# Revit family: Haworth_BeHold_Modular_AttachedLateral
name_source: partatom
category: Furniture Systems
revit_build: Autodesk Revit 2018 (Build: 20170223_1515(x64)
units: mm (PartAtom-declared; Revit-internal decimal feet)

## family parameters
Always vertical = Yes
Cut with Voids When Loaded = No
OmniClass Number = 23.40.70.14.64.21
OmniClass Title = Systems Furniture
Part Type = Normal
Room Calculation Point = No
Round Connector Dimension = Use Diameter
Shared = No
Work Plane-Based = No

## types (8) — shared parameters
16 Deep Leg = Yes
Actual D/T Leg Control = No
Actual Depth = 16"
Actual Width = 42"
Assembly Code = E2020200
Blade Pull = Yes
Blade Pull Length = 41 13/16"
Case Thickness = 3/4"
Classic Pull = No
Classic Pull Length = 6 3/4"
Cresent Pull = No
Custom Size = No
Description = Haworth - Be_Hold - Lateral
Double Unit Leg = No
Drawer Width = 41 7/8"
Glide Finish = Haworth _ Polymer _ Slate
Leg Height = 6"
Linear Pull = No
Linear Pull Length = 8"
Manufacturer = Haworth
Max. Depth = 16"
Max. Height = 42"
Max. Width = 42"
Min. Depth = 16"
Min. Height = 22"
Min. Width = 24"
Model = Haworth Be_Hold
Revision Number = 1
Single Unit Leg = Yes
Size = Verify Final Dim. w/ Haworth
Standard Widths = 24, 30, 36, 42 in.
Sustainability Info = https://www.haworth.com
Top Thickness = 3/4"
Triple Unit Leg = No
URL = www.haworth.com
URL - Product = https://www.haworth.com
Warranty = http://www.haworth.com
Width = 42"
Wing Pull = No
Wing Pull Length = 16 3/4"
With Lock = Yes

## per-type parameters (varying)
- B/B/F - Proud Back - 42w: Actual Height=28"; Actual Single Leg Control=No; Back Case Back Control=0"; Back Case Side Control=0"; Bottom Case Offset=1/2"; Bottom Drawer Height=13 1/8"; Bottom Drawer Lock Control=No; Bottom Drawer Offset=1 3/8"; Box Box File=Yes; Box File=No; Distance Between Drawer=1/4"; File File=No; File File File=No; Glide Control=Yes; Inset Style=No; Mid Drawer Lock Control=No; Middle Drawer Control=Yes; Middle Drawer Height=6 9/16"; Open with Box File=No; Open with File=No; Proud Style=Yes; Shelf Control=No; Shelf Offset=20"; Side Case Back Control=3/4"; Standard Storage Height=28"; Top Case Back Control=0"; Top Case Front Offset=0"; Top Drawer Control=Yes; Top Drawer Height=6 9/16"; Total Drawer Height=26 1/2"; With Leg=No
- B/F - Inset Back - 42w: Actual Height=22"; Actual Single Leg Control=No; Back Case Back Control=3/16"; Back Case Side Control=3/4"; Bottom Case Offset=1/2"; Bottom Drawer Height=13 149/256"; Bottom Drawer Lock Control=No; Bottom Drawer Offset=1 3/8"; Box Box File=No; Box File=Yes; Distance Between Drawer=1/8"; File File=No; File File File=No; Glide Control=Yes; Inset Style=Yes; Mid Drawer Lock Control=No; Middle Drawer Control=No; Middle Drawer Height=6 203/256"; Open with Box File=No; Open with File=No; Proud Style=No; Shelf Control=No; Shelf Offset=20 11/16"; Side Case Back Control=0"; Standard Storage Height=22"; Top Case Back Control=3/16"; Top Case Front Offset=0"; Top Drawer Control=Yes; Top Drawer Height=6 203/256"; Total Drawer Height=20 1/2"; With Leg=No
- O/F - Inset Back - 42w: Actual Height=22"; Actual Single Leg Control=No; Back Case Back Control=3/16"; Back Case Side Control=3/4"; Bottom Case Offset=1/2"; Bottom Drawer Height=13 149/256"; Bottom Drawer Lock Control=Yes; Bottom Drawer Offset=1 3/8"; Box Box File=No; Box File=No; Distance Between Drawer=1/8"; File File=No; File File File=No; Glide Control=Yes; Inset Style=Yes; Mid Drawer Lock Control=No; Middle Drawer Control=No; Middle Drawer Height=6 203/256"; Open with Box File=No; Open with File=Yes; Proud Style=No; Shelf Control=Yes; Shelf Offset=13 197/256"; Side Case Back Control=0"; Standard Storage Height=22"; Top Case Back Control=3/16"; Top Case Front Offset=2 1/4"; Top Drawer Control=No; Top Drawer Height=6 203/256"; Total Drawer Height=20 1/2"; With Leg=No
- O/B/F - Proud Back - 42w: Actual Height=28"; Actual Single Leg Control=No; Back Case Back Control=0"; Back Case Side Control=0"; Bottom Case Offset=1/2"; Bottom Drawer Height=13 1/8"; Bottom Drawer Lock Control=No; Bottom Drawer Offset=1 3/8"; Box Box File=No; Box File=No; Distance Between Drawer=1/4"; File File=No; File File File=No; Glide Control=Yes; Inset Style=No; Mid Drawer Lock Control=Yes; Middle Drawer Control=Yes; Middle Drawer Height=6 9/16"; Open with Box File=Yes; Open with File=No; Proud Style=Yes; Shelf Control=Yes; Shelf Offset=20"; Side Case Back Control=3/4"; Standard Storage Height=28"; Top Case Back Control=0"; Top Case Front Offset=2 1/4"; Top Drawer Control=No; Top Drawer Height=6 9/16"; Total Drawer Height=26 1/2"; With Leg=No
- F/F - Proud Back - 42w: Actual Height=28"; Actual Single Leg Control=No; Back Case Back Control=0"; Back Case Side Control=0"; Bottom Case Offset=1/2"; Bottom Drawer Height=13 3/16"; Bottom Drawer Lock Control=No; Bottom Drawer Offset=1 3/8"; Box Box File=No; Box File=No; Distance Between Drawer=1/8"; File File=Yes; File File File=No; Glide Control=Yes; Inset Style=No; Mid Drawer Lock Control=No; Middle Drawer Control=No; Middle Drawer Height=13 3/16"; Open with Box File=No; Open with File=No; Proud Style=Yes; Shelf Control=No; Shelf Offset=26 11/16"; Side Case Back Control=3/4"; Standard Storage Height=28"; Top Case Back Control=0"; Top Case Front Offset=0"; Top Drawer Control=Yes; Top Drawer Height=13 3/16"; Total Drawer Height=26 1/2"; With Leg=No
- F/F/F - Inset Back - 42w: Actual Height=42"; Actual Single Leg Control=No; Back Case Back Control=3/16"; Back Case Side Control=3/4"; Bottom Case Offset=1/2"; Bottom Drawer Height=13 107/256"; Bottom Drawer Lock Control=No; Bottom Drawer Offset=1 3/8"; Box Box File=No; Box File=No; Distance Between Drawer=1/4"; File File=No; File File File=Yes; Glide Control=Yes; Inset Style=Yes; Mid Drawer Lock Control=No; Middle Drawer Control=Yes; Middle Drawer Height=13 107/256"; Open with Box File=No; Open with File=No; Proud Style=No; Shelf Control=No; Shelf Offset=27 37/256"; Side Case Back Control=0"; Standard Storage Height=42"; Top Case Back Control=3/16"; Top Case Front Offset=0"; Top Drawer Control=Yes; Top Drawer Height=13 107/256"; Total Drawer Height=40 1/2"; With Leg=No
- O/F - Inset Back - 42w - With Leg: Actual Height=28"; Actual Single Leg Control=Yes; Back Case Back Control=3/16"; Back Case Side Control=3/4"; Bottom Case Offset=6"; Bottom Drawer Height=13 235/256"; Bottom Drawer Lock Control=Yes; Bottom Drawer Offset=6 7/8"; Box Box File=No; Box File=No; Distance Between Drawer=1/8"; File File=No; File File File=No; Glide Control=No; Inset Style=Yes; Mid Drawer Lock Control=No; Middle Drawer Control=No; Middle Drawer Height=6 245/256"; Open with Box File=No; Open with File=Yes; Proud Style=No; Shelf Control=Yes; Shelf Offset=14 27/256"; Side Case Back Control=0"; Standard Storage Height=22"; Top Case Back Control=3/16"; Top Case Front Offset=2 1/4"; Top Drawer Control=No; Top Drawer Height=6 245/256"; Total Drawer Height=21"; With Leg=Yes
- B/B/F - Proud Back - 42w - With Leg: Actual Height=34"; Actual Single Leg Control=Yes; Back Case Back Control=0"; Back Case Side Control=0"; Bottom Case Offset=6"; Bottom Drawer Height=13 3/8"; Bottom Drawer Lock Control=No; Bottom Drawer Offset=6 7/8"; Box Box File=Yes; Box File=No; Distance Between Drawer=1/4"; File File=No; File File File=No; Glide Control=No; Inset Style=No; Mid Drawer Lock Control=No; Middle Drawer Control=Yes; Middle Drawer Height=6 11/16"; Open with Box File=No; Open with File=No; Proud Style=Yes; Shelf Control=No; Shelf Offset=20 3/8"; Side Case Back Control=3/4"; Standard Storage Height=28"; Top Case Back Control=0"; Top Case Front Offset=0"; Top Drawer Control=Yes; Top Drawer Height=6 11/16"; Total Drawer Height=27"; With Leg=Yes

## geometry (parser evidence)
native form markers: Sweep x11
no freeform markers — native parametric forms only
